# Revit family: VTp735 Тройник переходной
name_source: partatom
category: Соединительные детали трубопроводов
revit_build: Autodesk Revit 2015 (Build: 20140606_1530(x64)
units: mm (PartAtom-declared; Revit-internal decimal feet)

## types (23) — shared parameters
Группа модели = VTp.700
Изготовитель = VALTEC S.R.L.
Коэффициент K = 0.5
Метод определения потерь = Коэффициент K
Описание = Тройник переходной
Таблица коэффициентов K = Angle Valve Threaded

## per-type parameters (varying)
- 25-20-20: 25-20-20=Да; 25-20-25=Нет; 32-20-20=Нет; 32-20-25=Нет; 32-20-32=Нет; 32-25-20=Нет; 32-25-25=Нет; 32-25-32=Нет; 40-20-40=Нет; 40-25-40=Нет; 40-32-40=Нет; 50-20-50=Нет; 50-25-50=Нет; 50-32-50=Нет; 50-40-50=Нет; 63-20-63=Нет; 63-25-63=Нет; 63-32-63=Нет; 63-40-63=Нет; 63-50-63=Нет; 75-40-75=Нет; 75-50-75=Нет; 75-63-75=Нет; A=55 мм; B=17 мм; C=15 мм; D=17 мм; d1=25 мм; d2=20 мм; d3=20 мм; Код по классификатору=VTp.735.0.025020020; Сц=28 мм
- 25-20-25: 25-20-20=Нет; 25-20-25=Да; 32-20-20=Нет; 32-20-25=Нет; 32-20-32=Нет; 32-25-20=Нет; 32-25-25=Нет; 32-25-32=Нет; 40-20-40=Нет; 40-25-40=Нет; 40-32-40=Нет; 50-20-50=Нет; 50-25-50=Нет; 50-32-50=Нет; 50-40-50=Нет; 63-20-63=Нет; 63-25-63=Нет; 63-32-63=Нет; 63-40-63=Нет; 63-50-63=Нет; 75-40-75=Нет; 75-50-75=Нет; 75-63-75=Нет; A=55 мм; B=17 мм; C=15 мм; D=17 мм; d1=25 мм; d2=20 мм; d3=25 мм; Код по классификатору=VTp.735.0.025020025; Сц=28 мм
- 32-20-20: 25-20-20=Нет; 25-20-25=Нет; 32-20-20=Да; 32-20-25=Нет; 32-20-32=Нет; 32-25-20=Нет; 32-25-25=Нет; 32-25-32=Нет; 40-20-40=Нет; 40-25-40=Нет; 40-32-40=Нет; 50-20-50=Нет; 50-25-50=Нет; 50-32-50=Нет; 50-40-50=Нет; 63-20-63=Нет; 63-25-63=Нет; 63-32-63=Нет; 63-40-63=Нет; 63-50-63=Нет; 75-40-75=Нет; 75-50-75=Нет; 75-63-75=Нет; A=60 мм; B=19 мм; C=15 мм; D=19 мм; d1=32 мм; d2=20 мм; d3=20 мм; Код по классификатору=VTp.735.0.032020020; Сц=32 мм
- 32-20-25: 25-20-20=Нет; 25-20-25=Нет; 32-20-20=Нет; 32-20-25=Да; 32-20-32=Нет; 32-25-20=Нет; 32-25-25=Нет; 32-25-32=Нет; 40-20-40=Нет; 40-25-40=Нет; 40-32-40=Нет; 50-20-50=Нет; 50-25-50=Нет; 50-32-50=Нет; 50-40-50=Нет; 63-20-63=Нет; 63-25-63=Нет; 63-32-63=Нет; 63-40-63=Нет; 63-50-63=Нет; 75-40-75=Нет; 75-50-75=Нет; 75-63-75=Нет; A=66 мм; B=19 мм; C=16 мм; D=17 мм; d1=32 мм; d2=20 мм; d3=25 мм; Код по классификатору=VTp.735.0.032020025; Сц=34 мм
- 32-20-32: 25-20-20=Нет; 25-20-25=Нет; 32-20-20=Нет; 32-20-25=Нет; 32-20-32=Да; 32-25-20=Нет; 32-25-25=Нет; 32-25-32=Нет; 40-20-40=Нет; 40-25-40=Нет; 40-32-40=Нет; 50-20-50=Нет; 50-25-50=Нет; 50-32-50=Нет; 50-40-50=Нет; 63-20-63=Нет; 63-25-63=Нет; 63-32-63=Нет; 63-40-63=Нет; 63-50-63=Нет; 75-40-75=Нет; 75-50-75=Нет; 75-63-75=Нет; A=60 мм; B=19 мм; C=15 мм; D=19 мм; d1=32 мм; d2=20 мм; d3=32 мм; Код по классификатору=VTp.735.0.032020032; Сц=32 мм
- 32-25-20: 25-20-20=Нет; 25-20-25=Нет; 32-20-20=Нет; 32-20-25=Нет; 32-20-32=Нет; 32-25-20=Да; 32-25-25=Нет; 32-25-32=Нет; 40-20-40=Нет; 40-25-40=Нет; 40-32-40=Нет; 50-20-50=Нет; 50-25-50=Нет; 50-32-50=Нет; 50-40-50=Нет; 63-20-63=Нет; 63-25-63=Нет; 63-32-63=Нет; 63-40-63=Нет; 63-50-63=Нет; 75-40-75=Нет; 75-50-75=Нет; 75-63-75=Нет; A=65 мм; B=19 мм; C=17 мм; D=15 мм; d1=32 мм; d2=25 мм; d3=20 мм; Код по классификатору=VTp.735.0.032025020; Сц=34 мм
- 32-25-25: 25-20-20=Нет; 25-20-25=Нет; 32-20-20=Нет; 32-20-25=Нет; 32-20-32=Нет; 32-25-20=Нет; 32-25-25=Да; 32-25-32=Нет; 40-20-40=Нет; 40-25-40=Нет; 40-32-40=Нет; 50-20-50=Нет; 50-25-50=Нет; 50-32-50=Нет; 50-40-50=Нет; 63-20-63=Нет; 63-25-63=Нет; 63-32-63=Нет; 63-40-63=Нет; 63-50-63=Нет; 75-40-75=Нет; 75-50-75=Нет; 75-63-75=Нет; A=66 мм; B=19 мм; C=17 мм; D=17 мм; d1=32 мм; d2=25 мм; d3=25 мм; Код по классификатору=VTp.735.0.032025025; Сц=34 мм
- 32-25-32: 25-20-20=Нет; 25-20-25=Нет; 32-20-20=Нет; 32-20-25=Нет; 32-20-32=Нет; 32-25-20=Нет; 32-25-25=Нет; 32-25-32=Да; 40-20-40=Нет; 40-25-40=Нет; 40-32-40=Нет; 50-20-50=Нет; 50-25-50=Нет; 50-32-50=Нет; 50-40-50=Нет; 63-20-63=Нет; 63-25-63=Нет; 63-32-63=Нет; 63-40-63=Нет; 63-50-63=Нет; 75-40-75=Нет; 75-50-75=Нет; 75-63-75=Нет; A=65 мм; B=19 мм; C=17 мм; D=19 мм; d1=32 мм; d2=25 мм; d3=32 мм; Код по классификатору=VTp.735.0.032025032; Сц=34 мм
- 40-20-40: 25-20-20=Нет; 25-20-25=Нет; 32-20-20=Нет; 32-20-25=Нет; 32-20-32=Нет; 32-25-20=Нет; 32-25-25=Нет; 32-25-32=Нет; 40-20-40=Да; 40-25-40=Нет; 40-32-40=Нет; 50-20-50=Нет; 50-25-50=Нет; 50-32-50=Нет; 50-40-50=Нет; 63-20-63=Нет; 63-25-63=Нет; 63-32-63=Нет; 63-40-63=Нет; 63-50-63=Нет; 75-40-75=Нет; 75-50-75=Нет; 75-63-75=Нет; A=75 мм; B=21 мм; C=15 мм; D=21 мм; d1=40 мм; d2=20 мм; d3=40 мм; Код по классификатору=VTp.735.0.040020040; Сц=39 мм
- 40-25-40: 25-20-20=Нет; 25-20-25=Нет; 32-20-20=Нет; 32-20-25=Нет; 32-20-32=Нет; 32-25-20=Нет; 32-25-25=Нет; 32-25-32=Нет; 40-20-40=Нет; 40-25-40=Да; 40-32-40=Нет; 50-20-50=Нет; 50-25-50=Нет; 50-32-50=Нет; 50-40-50=Нет; 63-20-63=Нет; 63-25-63=Нет; 63-32-63=Нет; 63-40-63=Нет; 63-50-63=Нет; 75-40-75=Нет; 75-50-75=Нет; 75-63-75=Нет; A=80 мм; B=21 мм; C=17 мм; D=21 мм; d1=40 мм; d2=25 мм; d3=40 мм; Код по классификатору=VTp.735.0.040025040; Сц=40 мм
- 40-32-40: 25-20-20=Нет; 25-20-25=Нет; 32-20-20=Нет; 32-20-25=Нет; 32-20-32=Нет; 32-25-20=Нет; 32-25-25=Нет; 32-25-32=Нет; 40-20-40=Нет; 40-25-40=Нет; 40-32-40=Да; 50-20-50=Нет; 50-25-50=Нет; 50-32-50=Нет; 50-40-50=Нет; 63-20-63=Нет; 63-25-63=Нет; 63-32-63=Нет; 63-40-63=Нет; 63-50-63=Нет; 75-40-75=Нет; 75-50-75=Нет; 75-63-75=Нет; A=87 мм; B=21 мм; C=19 мм; D=21 мм; d1=40 мм; d2=32 мм; d3=40 мм; Код по классификатору=VTp.735.0.040032040; Сц=41 мм
- 50-20-50: 25-20-20=Нет; 25-20-25=Нет; 32-20-20=Нет; 32-20-25=Нет; 32-20-32=Нет; 32-25-20=Нет; 32-25-25=Нет; 32-25-32=Нет; 40-20-40=Нет; 40-25-40=Нет; 40-32-40=Нет; 50-20-50=Да; 50-25-50=Нет; 50-32-50=Нет; 50-40-50=Нет; 63-20-63=Нет; 63-25-63=Нет; 63-32-63=Нет; 63-40-63=Нет; 63-50-63=Нет; 75-40-75=Нет; 75-50-75=Нет; 75-63-75=Нет; A=84 мм; B=24 мм; C=15 мм; D=24 мм; d1=50 мм; d2=20 мм; d3=50 мм; Код по классификатору=VTp.735.0.050020050; Сц=44 мм
- 50-25-50: 25-20-20=Нет; 25-20-25=Нет; 32-20-20=Нет; 32-20-25=Нет; 32-20-32=Нет; 32-25-20=Нет; 32-25-25=Нет; 32-25-32=Нет; 40-20-40=Нет; 40-25-40=Нет; 40-32-40=Нет; 50-20-50=Нет; 50-25-50=Да; 50-32-50=Нет; 50-40-50=Нет; 63-20-63=Нет; 63-25-63=Нет; 63-32-63=Нет; 63-40-63=Нет; 63-50-63=Нет; 75-40-75=Нет; 75-50-75=Нет; 75-63-75=Нет; A=88 мм; B=24 мм; C=17 мм; D=24 мм; d1=50 мм; d2=25 мм; d3=50 мм; Код по классификатору=VTp.735.0.050025050; Сц=45 мм
- 50-32-50: 25-20-20=Нет; 25-20-25=Нет; 32-20-20=Нет; 32-20-25=Нет; 32-20-32=Нет; 32-25-20=Нет; 32-25-25=Нет; 32-25-32=Нет; 40-20-40=Нет; 40-25-40=Нет; 40-32-40=Нет; 50-20-50=Нет; 50-25-50=Нет; 50-32-50=Да; 50-40-50=Нет; 63-20-63=Нет; 63-25-63=Нет; 63-32-63=Нет; 63-40-63=Нет; 63-50-63=Нет; 75-40-75=Нет; 75-50-75=Нет; 75-63-75=Нет; A=102 мм; B=24 мм; C=19 мм; D=24 мм; d1=50 мм; d2=32 мм; d3=50 мм; Код по классификатору=VTp.735.0.050032050; Сц=49 мм
- 50-40-50: 25-20-20=Нет; 25-20-25=Нет; 32-20-20=Нет; 32-20-25=Нет; 32-20-32=Нет; 32-25-20=Нет; 32-25-25=Нет; 32-25-32=Нет; 40-20-40=Нет; 40-25-40=Нет; 40-32-40=Нет; 50-20-50=Нет; 50-25-50=Нет; 50-32-50=Нет; 50-40-50=Да; 63-20-63=Нет; 63-25-63=Нет; 63-32-63=Нет; 63-40-63=Нет; 63-50-63=Нет; 75-40-75=Нет; 75-50-75=Нет; 75-63-75=Нет; A=102 мм; B=24 мм; C=21 мм; D=24 мм; d1=50 мм; d2=40 мм; d3=50 мм; Код по классификатору=VTp.735.0.050040050; Сц=51 мм
- 63-20-63: 25-20-20=Нет; 25-20-25=Нет; 32-20-20=Нет; 32-20-25=Нет; 32-20-32=Нет; 32-25-20=Нет; 32-25-25=Нет; 32-25-32=Нет; 40-20-40=Нет; 40-25-40=Нет; 40-32-40=Нет; 50-20-50=Нет; 50-25-50=Нет; 50-32-50=Нет; 50-40-50=Нет; 63-20-63=Да; 63-25-63=Нет; 63-32-63=Нет; 63-40-63=Нет; 63-50-63=Нет; 75-40-75=Нет; 75-50-75=Нет; 75-63-75=Нет; A=128 мм; B=26 мм; C=15 мм; D=26 мм; d1=63 мм; d2=20 мм; d3=63 мм; Код по классификатору=VTp.735.0.063020063; Сц=64 мм
- 63-25-63: 25-20-20=Нет; 25-20-25=Нет; 32-20-20=Нет; 32-20-25=Нет; 32-20-32=Нет; 32-25-20=Нет; 32-25-25=Нет; 32-25-32=Нет; 40-20-40=Нет; 40-25-40=Нет; 40-32-40=Нет; 50-20-50=Нет; 50-25-50=Нет; 50-32-50=Нет; 50-40-50=Нет; 63-20-63=Нет; 63-25-63=Да; 63-32-63=Нет; 63-40-63=Нет; 63-50-63=Нет; 75-40-75=Нет; 75-50-75=Нет; 75-63-75=Нет; A=128 мм; B=26 мм; C=17 мм; D=26 мм; d1=63 мм; d2=25 мм; d3=63 мм; Код по классификатору=VTp.735.0.063025063; Сц=64 мм
- 63-32-63: 25-20-20=Нет; 25-20-25=Нет; 32-20-20=Нет; 32-20-25=Нет; 32-20-32=Нет; 32-25-20=Нет; 32-25-25=Нет; 32-25-32=Нет; 40-20-40=Нет; 40-25-40=Нет; 40-32-40=Нет; 50-20-50=Нет; 50-25-50=Нет; 50-32-50=Нет; 50-40-50=Нет; 63-20-63=Нет; 63-25-63=Нет; 63-32-63=Да; 63-40-63=Нет; 63-50-63=Нет; 75-40-75=Нет; 75-50-75=Нет; 75-63-75=Нет; A=128 мм; B=26 мм; C=19 мм; D=26 мм; d1=63 мм; d2=32 мм; d3=63 мм; Код по классификатору=VTp.735.0.063032063; Сц=64 мм
- 63-40-63: 25-20-20=Нет; 25-20-25=Нет; 32-20-20=Нет; 32-20-25=Нет; 32-20-32=Нет; 32-25-20=Нет; 32-25-25=Нет; 32-25-32=Нет; 40-20-40=Нет; 40-25-40=Нет; 40-32-40=Нет; 50-20-50=Нет; 50-25-50=Нет; 50-32-50=Нет; 50-40-50=Нет; 63-20-63=Нет; 63-25-63=Нет; 63-32-63=Нет; 63-40-63=Да; 63-50-63=Нет; 75-40-75=Нет; 75-50-75=Нет; 75-63-75=Нет; A=128 мм; B=26 мм; C=21 мм; D=26 мм; d1=63 мм; d2=40 мм; d3=63 мм; Код по классификатору=VTp.735.0.063040063; Сц=64 мм
- 63-50-63: 25-20-20=Нет; 25-20-25=Нет; 32-20-20=Нет; 32-20-25=Нет; 32-20-32=Нет; 32-25-20=Нет; 32-25-25=Нет; 32-25-32=Нет; 40-20-40=Нет; 40-25-40=Нет; 40-32-40=Нет; 50-20-50=Нет; 50-25-50=Нет; 50-32-50=Нет; 50-40-50=Нет; 63-20-63=Нет; 63-25-63=Нет; 63-32-63=Нет; 63-40-63=Нет; 63-50-63=Да; 75-40-75=Нет; 75-50-75=Нет; 75-63-75=Нет; A=128 мм; B=26 мм; C=24 мм; D=26 мм; d1=63 мм; d2=50 мм; d3=63 мм; Код по классификатору=VTp.735.0.063050063; Сц=64 мм
- 75-40-75: 25-20-20=Нет; 25-20-25=Нет; 32-20-20=Нет; 32-20-25=Нет; 32-20-32=Нет; 32-25-20=Нет; 32-25-25=Нет; 32-25-32=Нет; 40-20-40=Нет; 40-25-40=Нет; 40-32-40=Нет; 50-20-50=Нет; 50-25-50=Нет; 50-32-50=Нет; 50-40-50=Нет; 63-20-63=Нет; 63-25-63=Нет; 63-32-63=Нет; 63-40-63=Нет; 63-50-63=Нет; 75-40-75=Да; 75-50-75=Нет; 75-63-75=Нет; A=146 мм; B=35 мм; C=21 мм; D=35 мм; d1=75 мм; d2=40 мм; d3=75 мм; Код по классификатору=VTp.735.0.075040075; Сц=73 мм
- 75-50-75: 25-20-20=Нет; 25-20-25=Нет; 32-20-20=Нет; 32-20-25=Нет; 32-20-32=Нет; 32-25-20=Нет; 32-25-25=Нет; 32-25-32=Нет; 40-20-40=Нет; 40-25-40=Нет; 40-32-40=Нет; 50-20-50=Нет; 50-25-50=Нет; 50-32-50=Нет; 50-40-50=Нет; 63-20-63=Нет; 63-25-63=Нет; 63-32-63=Нет; 63-40-63=Нет; 63-50-63=Нет; 75-40-75=Нет; 75-50-75=Да; 75-63-75=Нет; A=146 мм; B=35 мм; C=24 мм; D=35 мм; d1=75 мм; d2=50 мм; d3=75 мм; Код по классификатору=VTp.735.0.075050075; Сц=73 мм
- 75-63-75: 25-20-20=Нет; 25-20-25=Нет; 32-20-20=Нет; 32-20-25=Нет; 32-20-32=Нет; 32-25-20=Нет; 32-25-25=Нет; 32-25-32=Нет; 40-20-40=Нет; 40-25-40=Нет; 40-32-40=Нет; 50-20-50=Нет; 50-25-50=Нет; 50-32-50=Нет; 50-40-50=Нет; 63-20-63=Нет; 63-25-63=Нет; 63-32-63=Нет; 63-40-63=Нет; 63-50-63=Нет; 75-40-75=Нет; 75-50-75=Нет; 75-63-75=Да; A=146 мм; B=35 мм; C=26 мм; D=35 мм; d1=75 мм; d2=63 мм; d3=75 мм; Код по классификатору=VTp.735.0.075063075; Сц=73 мм
